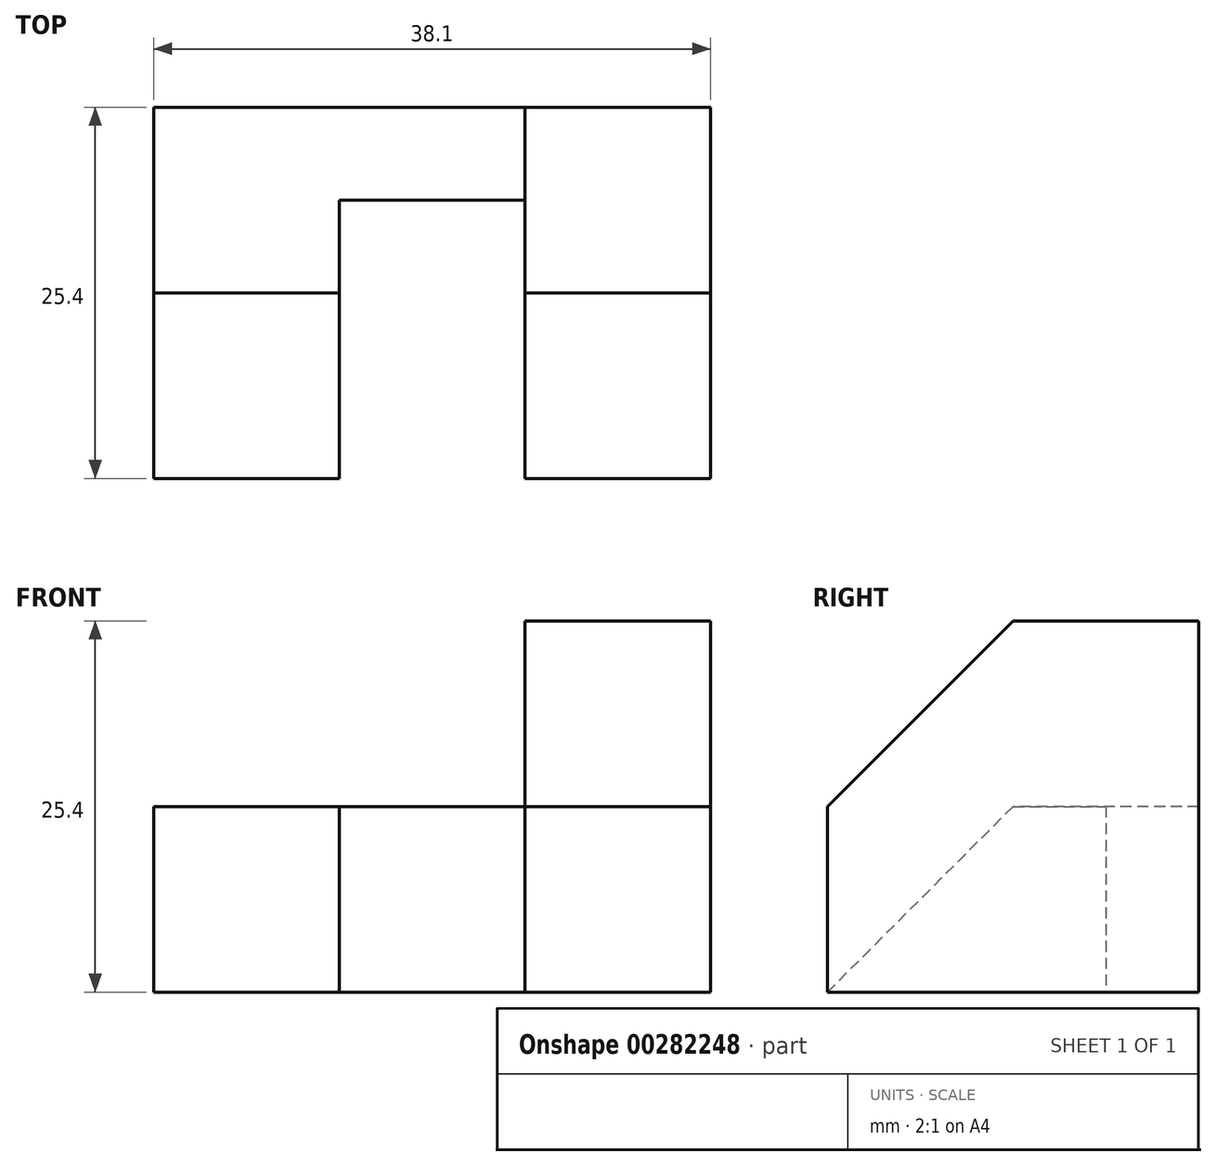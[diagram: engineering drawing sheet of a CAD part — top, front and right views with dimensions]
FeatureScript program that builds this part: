
annotation { "Feature Type Name" : "Feature", "Feature Type Description" : "" }
export const myFeature = defineFeature(function(context is Context, id is Id, definition is map)
    precondition{}
    {
        {
            var Q0;
            Q0=qCreatedBy(makeId("Right.planeOp"),FACE);
            var sketch = newSketch(context, id + "F0", { "sketchPlane" : qUnion([Q0])});
            skLineSegment(sketch, "E0.bottom", {"start": v(0, 0) * mm, "end": v(-25.4, 0) * mm});
            skLineSegment(sketch, "E0.top", {"start": v(0, 25.4) * mm, "end": v(-25.4, 25.4) * mm});
            skLineSegment(sketch, "E0.left", {"start": v(0, 0) * mm, "end": v(0, 25.4) * mm});
            skLineSegment(sketch, "E0.right", {"start": v(-25.4, 0) * mm, "end": v(-25.4, 25.4) * mm});
            skSolve(sketch);
        }
        {
            var Q0;
            Q0 = qSketchRegion(id + "F0", true);
            extrude(context, id + "F1", {"entities" : qUnion([Q0]), "depth" : 12.7 * mm});
        }
        {
            var Q0;
            Q0=qCreatedBy(makeId("Right.planeOp"),FACE);
            var sketch = newSketch(context, id + "F2", { "sketchPlane" : qUnion([Q0])});
            skLineSegment(sketch, "E1", {"start": v(-25.4, 25.4) * mm, "end": v(-25.4, 12.7) * mm});
            skLineSegment(sketch, "E2", {"start": v(-25.4, 12.7) * mm, "end": v(-25.4, 25.4) * mm});
            skLineSegment(sketch, "E3", {"start": v(-12.7, 25.4) * mm, "end": v(-25.4, 25.4) * mm});
            skLineSegment(sketch, "E4", {"start": v(-25.4, 12.7) * mm, "end": v(-12.7, 25.4) * mm});
            skSolve(sketch);
        }
        {
            var Q0;
            Q0 = qSketchRegion(id + "F2", true);
            extrude(context, id + "F3", {"entities" : qUnion([Q0]), "operationType" : NewBodyOperationType.REMOVE, "depth" : 12.7 * mm});
        }
        {
            var Q0;
            Q0=makeQuery(id+"F1.opExtrude","CAP_FACE",FACE,{"disambiguationData":[OSD([sQuery(id+"F0.wireOp",EDGE,"E0.bottom"),sQuery(id+"F0.wireOp",EDGE,"E0.top"),sQuery(id+"F0.wireOp",EDGE,"E0.left"),sQuery(id+"F0.wireOp",EDGE,"E0.right")])],"isStart":true});
            var sketch = newSketch(context, id + "F4", { "sketchPlane" : qUnion([Q0])});
            skLineSegment(sketch, "E5.bottom", {"start": v(0, 0) * mm, "end": v(6.35, 0) * mm});
            skLineSegment(sketch, "E5.top", {"start": v(0, 12.7) * mm, "end": v(6.35, 12.7) * mm});
            skLineSegment(sketch, "E5.left", {"start": v(0, 0) * mm, "end": v(0, 12.7) * mm});
            skLineSegment(sketch, "E5.right", {"start": v(6.35, 0) * mm, "end": v(6.35, 12.7) * mm});
            skSolve(sketch);
        }
        {
            var Q0;
            Q0 = qSketchRegion(id + "F4", true);
            extrude(context, id + "F5", {"entities" : qUnion([Q0]), "operationType" : NewBodyOperationType.ADD, "depth" : 25.4 * mm});
        }
        {
            var Q0;
            Q0=makeQuery(id+"F5.opExtrude","SWEPT_FACE",FACE,{"disambiguationData":[OSD([sQuery(id+"F4.wireOp",EDGE,"E5.right")])]});
            var sketch = newSketch(context, id + "F6", { "sketchPlane" : qUnion([Q0])});
            skLineSegment(sketch, "E6.bottom", {"start": v(-25.4, 12.7) * mm, "end": v(-12.7, 12.7) * mm});
            skLineSegment(sketch, "E6.top", {"start": v(-25.4, 0) * mm, "end": v(-12.7, 0) * mm});
            skLineSegment(sketch, "E6.left", {"start": v(-25.4, 12.7) * mm, "end": v(-25.4, 0) * mm});
            skLineSegment(sketch, "E6.right", {"start": v(-12.7, 12.7) * mm, "end": v(-12.7, 0) * mm});
            skSolve(sketch);
        }
        {
            var Q0;
            Q0 = qSketchRegion(id + "F6", true);
            extrude(context, id + "F7", {"entities" : qUnion([Q0]), "operationType" : NewBodyOperationType.ADD, "depth" : 19.05 * mm});
        }
        {
            var Q0;
            Q0=makeQuery(id+"F7.boolean.opBoolean","MERGE",FACE,{"derivedFrom":[makeQuery(id+"F5.opExtrude","CAP_FACE",FACE,{"disambiguationData":[OSD([sQuery(id+"F4.wireOp",EDGE,"E5.bottom"),sQuery(id+"F4.wireOp",EDGE,"E5.top"),sQuery(id+"F4.wireOp",EDGE,"E5.left"),sQuery(id+"F4.wireOp",EDGE,"E5.right")])],"isStart":false}),makeQuery(id+"F7.opExtrude","SWEPT_FACE",FACE,{"disambiguationData":[OSD([sQuery(id+"F6.wireOp",EDGE,"E6.left")])]})]});
            var sketch = newSketch(context, id + "F8", { "sketchPlane" : qUnion([Q0])});
            skLineSegment(sketch, "E7", {"start": v(12.7, 12.7) * mm, "end": v(25.4, 0) * mm});
            skLineSegment(sketch, "E8", {"start": v(25.4, 0) * mm, "end": v(25.4, 12.7) * mm});
            skLineSegment(sketch, "E9", {"start": v(25.4, 12.7) * mm, "end": v(12.7, 12.7) * mm});
            skSolve(sketch);
        }
        {
            var Q0;
            Q0 = qSketchRegion(id + "F8", true);
            extrude(context, id + "F9", {"entities" : qUnion([Q0]), "operationType" : NewBodyOperationType.REMOVE, "oppositeDirection" : true, "depth" : 12.7 * mm});
        }
    });
